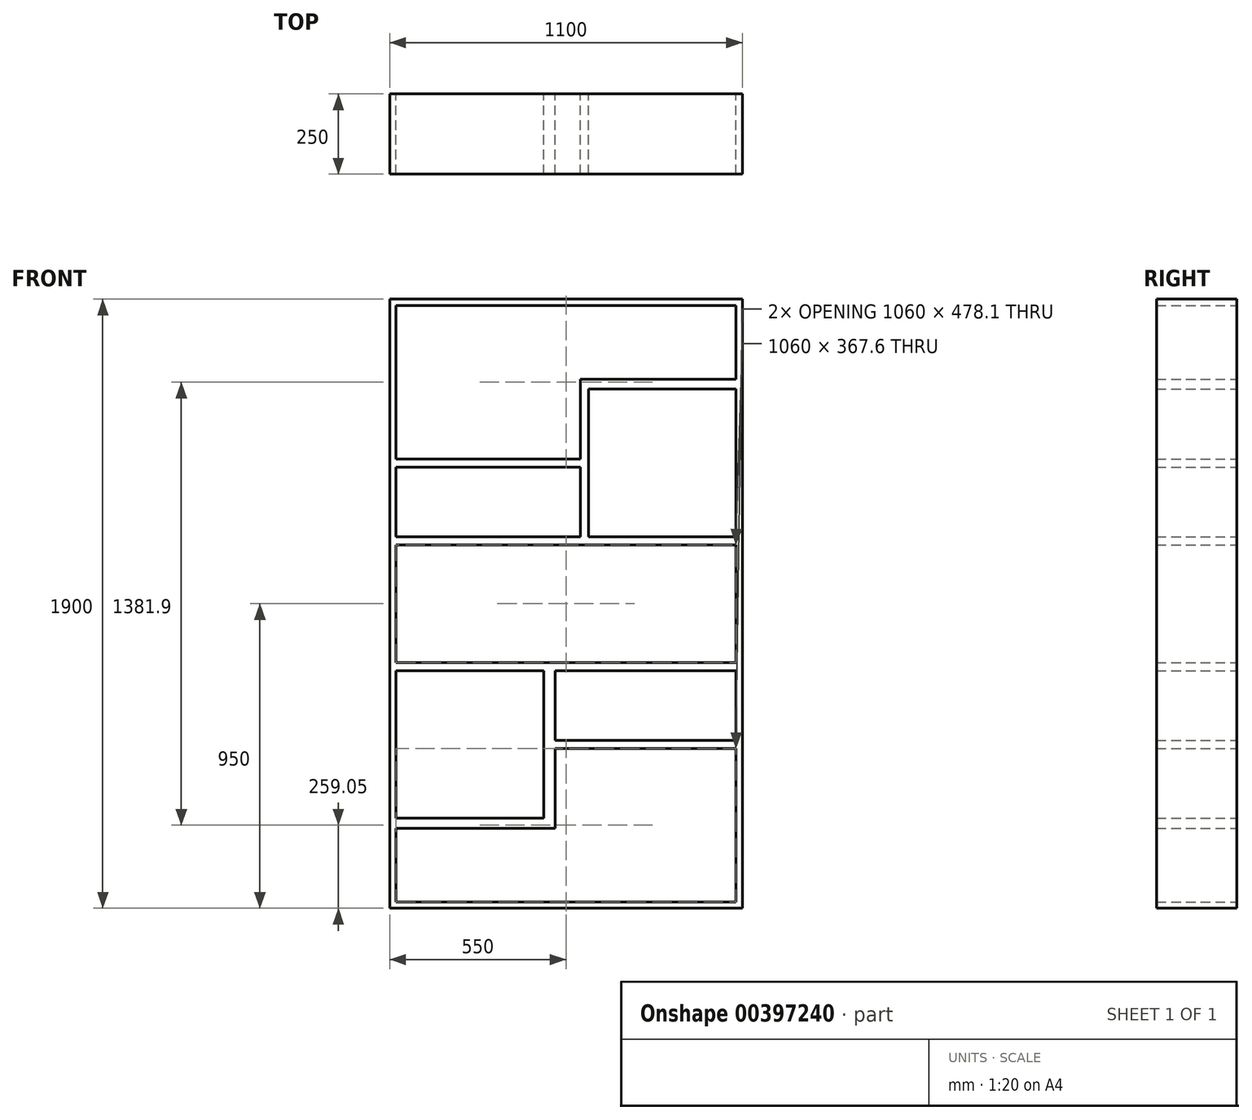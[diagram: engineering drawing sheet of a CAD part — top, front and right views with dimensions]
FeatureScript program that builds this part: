
annotation { "Feature Type Name" : "Feature", "Feature Type Description" : "" }
export const myFeature = defineFeature(function(context is Context, id is Id, definition is map)
    precondition{}
    {
        {
            var Q0;
            Q0=qCreatedBy(makeId("Front.planeOp"),FACE);
            var sketch = newSketch(context, id + "F0", { "sketchPlane" : qUnion([Q0])});
            skLineSegment(sketch, "E0.bottom", {"start": v(-550, -950) * mm, "end": v(550, -950) * mm});
            skLineSegment(sketch, "E0.top", {"start": v(-550, 950) * mm, "end": v(550, 950) * mm});
            skLineSegment(sketch, "E0.left", {"start": v(-550, -950) * mm, "end": v(-550, 950) * mm});
            skLineSegment(sketch, "E0.right", {"start": v(550, -950) * mm, "end": v(550, 950) * mm});
            skPoint(sketch, "E0.middle", {"position": v(0, 0) * mm});
            skLineSegment(sketch, "E1.bottom", {"start": v(-530, -930) * mm, "end": v(530, -930) * mm});
            skLineSegment(sketch, "E1.top", {"start": v(-530, 930) * mm, "end": v(530, 930) * mm});
            skLineSegment(sketch, "E1.left", {"start": v(-530, -930) * mm, "end": v(-530, 930) * mm});
            skLineSegment(sketch, "E1.right", {"start": v(530, -930) * mm, "end": v(530, 930) * mm});
            skSolve(sketch);
        }
        {
            var Q0;
            Q0 = qSketchRegion(id + "F0", true);
            extrude(context, id + "F1", {"entities" : qUnion([Q0]), "depth" : 250 * mm});
        }
        {
            var Q0;
            Q0=makeQuery(id+"F1.opExtrude","CAP_FACE",FACE,{"disambiguationData":[OSD([sQuery(id+"F0.wireOp",EDGE,"E0.bottom"),sQuery(id+"F0.wireOp",EDGE,"E0.top"),sQuery(id+"F0.wireOp",EDGE,"E0.left"),sQuery(id+"F0.wireOp",EDGE,"E0.right"),sQuery(id+"F0.wireOp",EDGE,"E1.bottom"),sQuery(id+"F0.wireOp",EDGE,"E1.top"),sQuery(id+"F0.wireOp",EDGE,"E1.left"),sQuery(id+"F0.wireOp",EDGE,"E1.right")])],"isStart":true});
            var sketch = newSketch(context, id + "F2", { "sketchPlane" : qUnion([Q0])});
            skLineSegment(sketch, "E2", {"start": v(530, 451.9) * mm, "end": v(-44.6, 451.9) * mm});
            skLineSegment(sketch, "E3", {"start": v(-44.6, 451.9) * mm, "end": v(-44.6, 700) * mm});
            skLineSegment(sketch, "E4", {"start": v(-44.6, 700) * mm, "end": v(-530, 700) * mm});
            skLineSegment(sketch, "E5", {"start": v(530, 426.5) * mm, "end": v(-44.6, 426.5) * mm});
            skLineSegment(sketch, "E6", {"start": v(-44.6, 426.5) * mm, "end": v(-44.6, 183.8) * mm});
            skLineSegment(sketch, "E7", {"start": v(-44.6, 183.8) * mm, "end": v(-530, 183.8) * mm});
            skLineSegment(sketch, "E8", {"start": v(-530, 669.2) * mm, "end": v(-70, 669.2) * mm});
            skLineSegment(sketch, "E9", {"start": v(-70, 669.2) * mm, "end": v(-70, 209.2) * mm});
            skLineSegment(sketch, "E10", {"start": v(-70, 209.2) * mm, "end": v(-530, 209.2) * mm});
            skLineSegment(sketch, "E11", {"start": v(-44.6, 426.5) * mm, "end": v(-44.6, 451.9) * mm, "construction": true});
            skLineSegment(sketch, "E12", {"start": v(-70, 439.2) * mm, "end": v(-44.6, 439.2) * mm, "construction": true});
            skLineSegment(sketch, "E13", {"start": v(530, 451.9) * mm, "end": v(530, 426.5) * mm});
            skLineSegment(sketch, "E14", {"start": v(-530, 700) * mm, "end": v(-530, 669.2) * mm});
            skLineSegment(sketch, "E15", {"start": v(-530, 209.2) * mm, "end": v(-530, 183.8) * mm});
            skLineSegment(sketch, "E16", {"start": v(-530, -451.9) * mm, "end": v(33.8, -451.9) * mm});
            skLineSegment(sketch, "E17", {"start": v(33.8, -451.9) * mm, "end": v(33.8, -700) * mm});
            skLineSegment(sketch, "E18", {"start": v(33.8, -700) * mm, "end": v(530, -700) * mm});
            skLineSegment(sketch, "E19", {"start": v(-530, -426.5) * mm, "end": v(33.8, -426.5) * mm});
            skLineSegment(sketch, "E20", {"start": v(33.8, -426.5) * mm, "end": v(33.8, -183.8) * mm});
            skLineSegment(sketch, "E21", {"start": v(33.8, -183.8) * mm, "end": v(530, -183.8) * mm});
            skLineSegment(sketch, "E22", {"start": v(530, -669.2) * mm, "end": v(70, -669.2) * mm});
            skLineSegment(sketch, "E23", {"start": v(70, -669.2) * mm, "end": v(70, -209.2) * mm});
            skLineSegment(sketch, "E24", {"start": v(70, -209.2) * mm, "end": v(530, -209.2) * mm});
            skLineSegment(sketch, "E25", {"start": v(33.8, -426.5) * mm, "end": v(33.8, -451.9) * mm, "construction": true});
            skLineSegment(sketch, "E26", {"start": v(70, -439.2) * mm, "end": v(33.8, -439.2) * mm, "construction": true});
            skLineSegment(sketch, "E27", {"start": v(-530, -451.9) * mm, "end": v(-530, -426.5) * mm});
            skLineSegment(sketch, "E28", {"start": v(530, -700) * mm, "end": v(530, -669.2) * mm});
            skLineSegment(sketch, "E29", {"start": v(530, -209.2) * mm, "end": v(530, -183.8) * mm});
            skLineSegment(sketch, "E30", {"start": v(-44.6, 183.8) * mm, "end": v(530, 183.8) * mm});
            skLineSegment(sketch, "E31", {"start": v(530, 183.8) * mm, "end": v(530, 209.2) * mm});
            skLineSegment(sketch, "E32", {"start": v(530, 209.2) * mm, "end": v(-44.6, 209.2) * mm});
            skLineSegment(sketch, "E33", {"start": v(33.8, -183.8) * mm, "end": v(-530, -183.8) * mm});
            skLineSegment(sketch, "E34", {"start": v(-530, -183.8) * mm, "end": v(-530, -209.2) * mm});
            skLineSegment(sketch, "E35", {"start": v(-530, -209.2) * mm, "end": v(33.8, -209.2) * mm});
            skSolve(sketch);
        }
        {
            var Q0;
            Q0 = qSketchRegion(id + "F2", true);
            var Q1;
            Q1=makeQuery(id+"F1.opExtrude","CAP_FACE",FACE,{"disambiguationData":[OSD([sQuery(id+"F0.wireOp",EDGE,"E0.bottom"),sQuery(id+"F0.wireOp",EDGE,"E0.top"),sQuery(id+"F0.wireOp",EDGE,"E0.left"),sQuery(id+"F0.wireOp",EDGE,"E0.right"),sQuery(id+"F0.wireOp",EDGE,"E1.bottom"),sQuery(id+"F0.wireOp",EDGE,"E1.top"),sQuery(id+"F0.wireOp",EDGE,"E1.left"),sQuery(id+"F0.wireOp",EDGE,"E1.right")])],"isStart":false});
            extrude(context, id + "F3", {"entities" : qUnion([Q0]), "operationType" : NewBodyOperationType.ADD, "endBound" : BoundingType.UP_TO_SURFACE, "oppositeDirection" : true, "endBoundEntityFace" : qUnion([Q1]), "depth" : 25 * mm});
        }
    });
